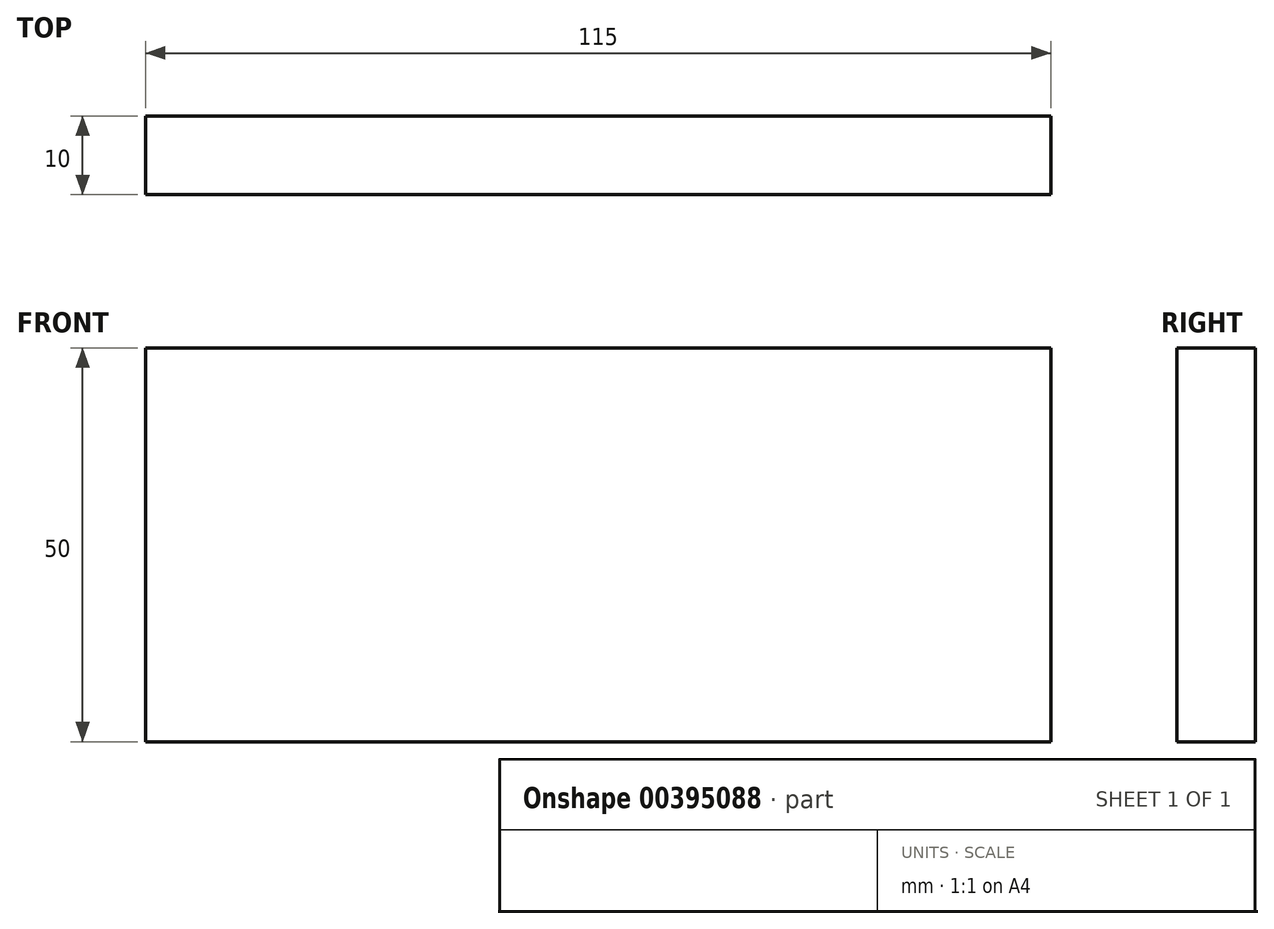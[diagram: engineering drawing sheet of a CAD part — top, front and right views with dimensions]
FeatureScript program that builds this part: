
annotation { "Feature Type Name" : "Feature", "Feature Type Description" : "" }
export const myFeature = defineFeature(function(context is Context, id is Id, definition is map)
    precondition{}
    {
        {
            var Q0;
            Q0=qCreatedBy(makeId("Front.planeOp"),FACE);
            var sketch = newSketch(context, id + "F0", { "sketchPlane" : qUnion([Q0])});
            skLineSegment(sketch, "E0.bottom", {"start": v(-57.5, -25) * mm, "end": v(57.5, -25) * mm});
            skLineSegment(sketch, "E0.top", {"start": v(-57.5, 25) * mm, "end": v(57.5, 25) * mm});
            skLineSegment(sketch, "E0.left", {"start": v(-57.5, -25) * mm, "end": v(-57.5, 25) * mm});
            skLineSegment(sketch, "E0.right", {"start": v(57.5, -25) * mm, "end": v(57.5, 25) * mm});
            skPoint(sketch, "E0.middle", {"position": v(0, 0) * mm});
            skSolve(sketch);
        }
        {
            var Q0;
            Q0 = qSketchRegion(id + "F0", true);
            extrude(context, id + "F1", {"entities" : qUnion([Q0]), "depth" : 10 * mm});
        }
    });
